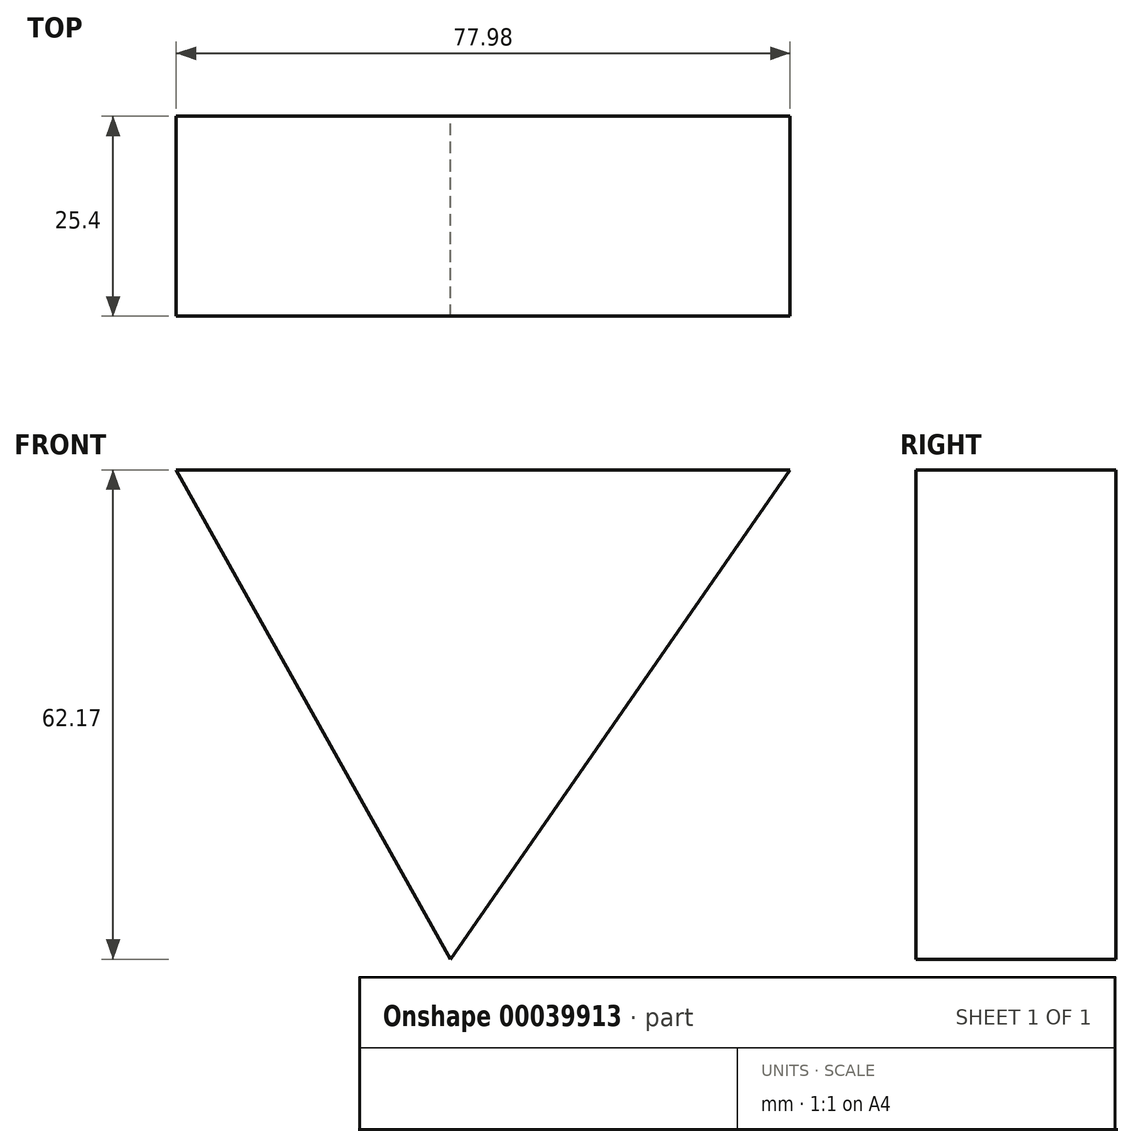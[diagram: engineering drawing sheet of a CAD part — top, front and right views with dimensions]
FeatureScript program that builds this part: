
annotation { "Feature Type Name" : "Feature", "Feature Type Description" : "" }
export const myFeature = defineFeature(function(context is Context, id is Id, definition is map)
    precondition{}
    {
        {
            var Q0;
            Q0=qCreatedBy(makeId("Front.planeOp"),FACE);
            var sketch = newSketch(context, id + "F0", { "sketchPlane" : qUnion([Q0])});
            skLineSegment(sketch, "E0", {"start": v(-58, 54.59) * mm, "end": v(19.98, 54.59) * mm});
            skLineSegment(sketch, "E1", {"start": v(19.98, 54.59) * mm, "end": v(-23.18, -7.58) * mm});
            skLineSegment(sketch, "E2", {"start": v(-23.18, -7.58) * mm, "end": v(-58, 54.59) * mm});
            skSolve(sketch);
        }
        {
            var Q0;
            Q0=makeQuery(id+"F0.imprint","IMPRINT",FACE,{"disambiguationData":[TD([[makeQuery(id+"F0.imprint","IMPRINT",EDGE,{"derivedFrom":sQuery(id+"F0.wireOp",EDGE,"E0")}),-1.0]])]});
            extrude(context, id + "F1", {"entities" : qUnion([Q0]), "depth" : 25.4 * mm});
        }
    });
